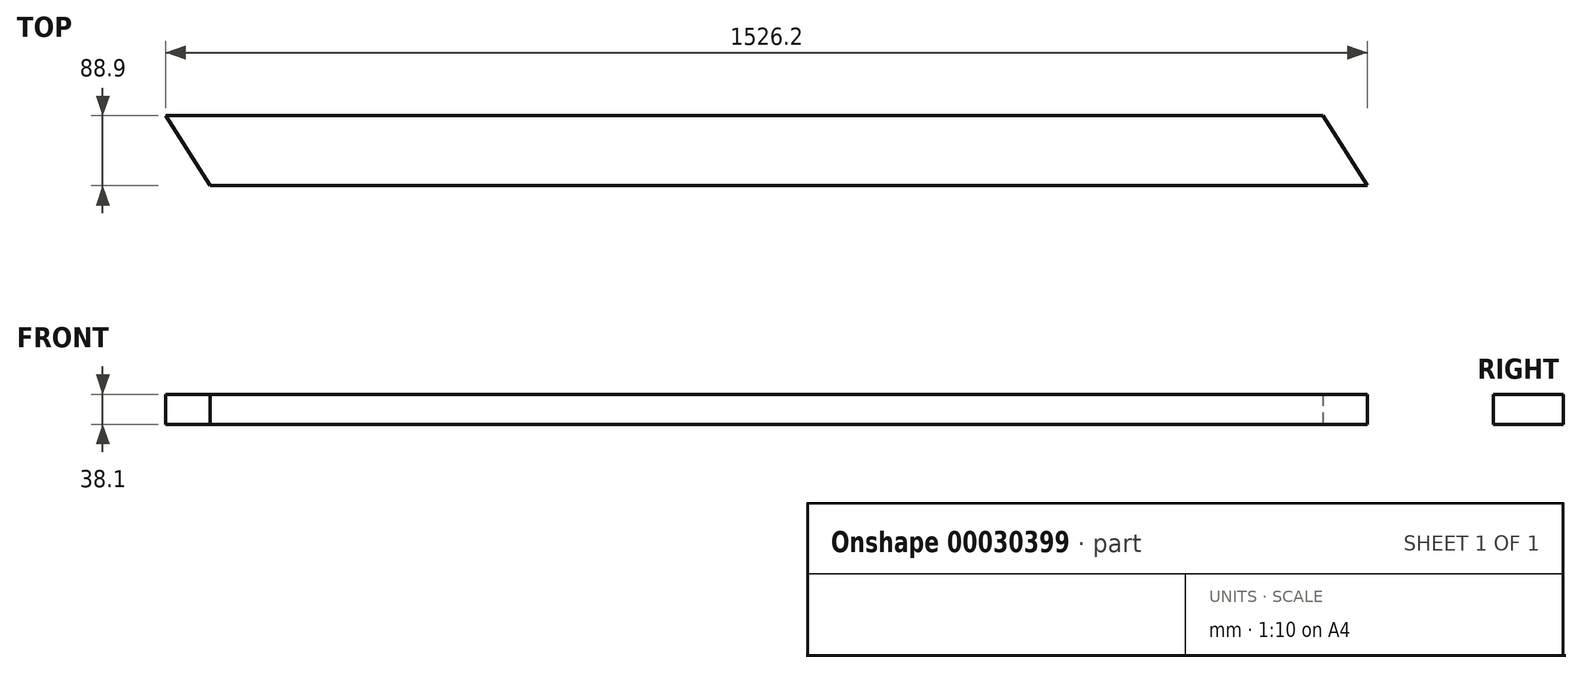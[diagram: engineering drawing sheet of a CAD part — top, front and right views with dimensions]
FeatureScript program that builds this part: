
annotation { "Feature Type Name" : "Feature", "Feature Type Description" : "" }
export const myFeature = defineFeature(function(context is Context, id is Id, definition is map)
    precondition{}
    {
        {
            var Q0;
            Q0=qCreatedBy(makeId("Top.planeOp"),FACE);
            var sketch = newSketch(context, id + "F0", { "sketchPlane" : qUnion([Q0])});
            skLineSegment(sketch, "E0.rect.left", {"start": v(763.1, 44.45) * mm, "end": v(763.1, -44.45) * mm, "construction": true});
            skLineSegment(sketch, "E0.rect.right", {"start": v(-763.1, 44.45) * mm, "end": v(-763.1, -44.45) * mm, "construction": true});
            skPoint(sketch, "E0.rect.middle", {"position": v(0, 0) * mm});
            skLineSegment(sketch, "E1", {"start": v(763.1, -44.45) * mm, "end": v(707.03, 44.45) * mm});
            skLineSegment(sketch, "E2", {"start": v(763.1, 44.45) * mm, "end": v(707.03, 44.45) * mm, "construction": true});
            skLineSegment(sketch, "E3", {"start": v(-763.1, 44.45) * mm, "end": v(707.03, 44.45) * mm});
            skLineSegment(sketch, "E4", {"start": v(-763.1, 44.45) * mm, "end": v(-707.03, -44.45) * mm});
            skLineSegment(sketch, "E5", {"start": v(-763.1, -44.45) * mm, "end": v(-707.03, -44.45) * mm, "construction": true});
            skLineSegment(sketch, "E6", {"start": v(763.1, -44.45) * mm, "end": v(-707.03, -44.45) * mm});
            skSolve(sketch);
        }
        {
            var Q0;
            Q0=qSketchRegion(id+"F0",true);
            extrude(context, id + "F1", {"entities" : qUnion([Q0]), "endBound" : BoundingType.SYMMETRIC, "depth" : 38.1 * mm});
        }
    });
